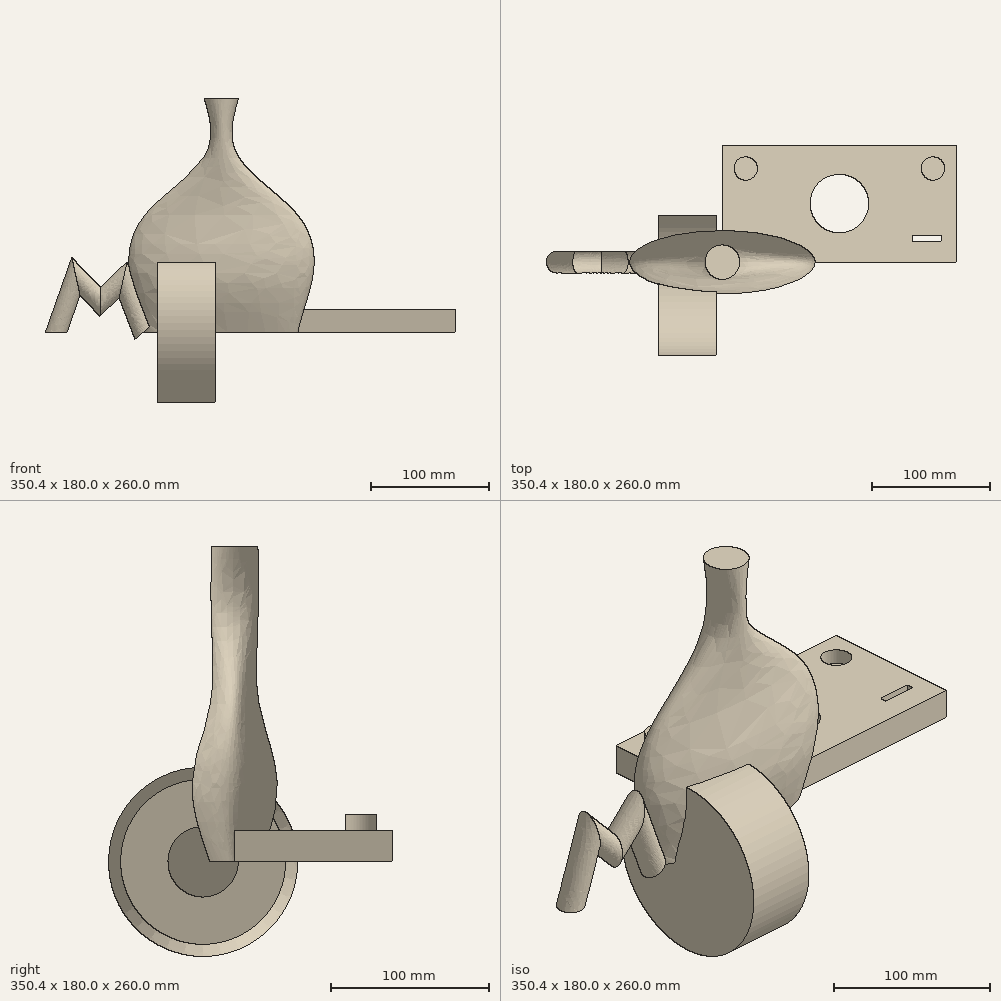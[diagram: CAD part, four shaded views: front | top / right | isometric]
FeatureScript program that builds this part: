
annotation { "Feature Type Name" : "Feature", "Feature Type Description" : "" }
export const myFeature = defineFeature(function(context is Context, id is Id, definition is map)
    precondition{}
    {
        {
            var Q0;
            Q0=qCreatedBy(makeId("Top.planeOp"),FACE);
            var sketch = newSketch(context, id + "F0", { "sketchPlane" : qUnion([Q0])});
            skLineSegment(sketch, "E0.bottom", {"start": v(0, 100) * mm, "end": v(200, 100) * mm});
            skLineSegment(sketch, "E0.top", {"start": v(0, 0) * mm, "end": v(200, 0) * mm});
            skLineSegment(sketch, "E0.left", {"start": v(0, 100) * mm, "end": v(0, 0) * mm});
            skLineSegment(sketch, "E0.right", {"start": v(200, 100) * mm, "end": v(200, 0) * mm});
            skCircle(sketch, "E1", {"center": v(100, 50) * mm, "radius": 25 * mm});
            skSolve(sketch);
        }
        {
            var Q0;
            Q0 = qSketchRegion(id + "F0", true);
            extrude(context, id + "F1", {"entities" : qUnion([Q0]), "depth" : 20 * mm});
        }
        {
            var Q0;
            Q0=makeQuery(id+"F1.opExtrude","CAP_FACE",FACE,{"disambiguationData":[OSD([sQuery(id+"F0.wireOp",EDGE,"E0.bottom"),sQuery(id+"F0.wireOp",EDGE,"E0.top"),sQuery(id+"F0.wireOp",EDGE,"E0.left"),sQuery(id+"F0.wireOp",EDGE,"E0.right"),sQuery(id+"F0.wireOp",EDGE,"E1")])],"isStart":false});
            var sketch = newSketch(context, id + "F2", { "sketchPlane" : qUnion([Q0])});
            skCircle(sketch, "E2", {"center": v(180, 80) * mm, "radius": 10 * mm});
            skSolve(sketch);
        }
        {
            var Q0;
            Q0=makeQuery(id+"F2.imprint","IMPRINT",FACE,{"disambiguationData":[TD([[makeQuery(id+"F2.imprint","IMPRINT",EDGE,{"derivedFrom":sQuery(id+"F2.wireOp",EDGE,"E2")}),1.0]])]});
            extrude(context, id + "F3", {"entities" : qUnion([Q0]), "operationType" : NewBodyOperationType.REMOVE, "oppositeDirection" : true, "depth" : 10 * mm});
        }
        {
            var Q0;
            Q0=makeQuery(id+"F1.opExtrude","CAP_FACE",FACE,{"disambiguationData":[OSD([sQuery(id+"F0.wireOp",EDGE,"E0.bottom"),sQuery(id+"F0.wireOp",EDGE,"E0.top"),sQuery(id+"F0.wireOp",EDGE,"E0.left"),sQuery(id+"F0.wireOp",EDGE,"E0.right"),sQuery(id+"F0.wireOp",EDGE,"E1")])],"isStart":false});
            var sketch = newSketch(context, id + "F4", { "sketchPlane" : qUnion([Q0])});
            skCircle(sketch, "E3", {"center": v(20, 80) * mm, "radius": 10 * mm});
            skSolve(sketch);
        }
        {
            var Q0;
            Q0=makeQuery(id+"F4.imprint","IMPRINT",FACE,{"disambiguationData":[TD([[makeQuery(id+"F4.imprint","IMPRINT",EDGE,{"derivedFrom":sQuery(id+"F4.wireOp",EDGE,"E3")}),1.0]])]});
            extrude(context, id + "F5", {"entities" : qUnion([Q0]), "operationType" : NewBodyOperationType.ADD, "depth" : 10 * mm});
        }
        {
            var Q0;
            Q0=qCreatedBy(makeId("Top.planeOp"),FACE);
            var sketch = newSketch(context, id + "F6", { "sketchPlane" : qUnion([Q0])});
            skLineSegment(sketch, "E4", {"start": v(-20, -20) * mm, "end": v(-55, -20) * mm});
            skLineSegment(sketch, "E5", {"start": v(-55, -20) * mm, "end": v(-55, -80) * mm});
            skLineSegment(sketch, "E6", {"start": v(-55, -80) * mm, "end": v(-5, -80) * mm});
            skLineSegment(sketch, "E7", {"start": v(-5, -80) * mm, "end": v(-49, -72.32) * mm});
            skLineSegment(sketch, "E8", {"start": v(-49, -72.32) * mm, "end": v(-49, -42.32) * mm});
            skArc(sketch, "E9", {"start": v(-20, -20) * mm, "mid": v(-38.3, -26.23) * mm, "end": v(-49, -42.32) * mm});
            skSolve(sketch);
        }
        {
            var Q0;
            Q0=makeQuery(id+"F6.imprint","IMPRINT",FACE,{"disambiguationData":[TD([[makeQuery(id+"F6.imprint","IMPRINT",EDGE,{"derivedFrom":sQuery(id+"F6.wireOp",EDGE,"E4")}),1.0]])]});
            var Q1;
            Q1=sQuery(id+"F6.wireOp",EDGE,"E4");
            revolve(context, id + "F7", {"entities" : qUnion([Q0]), "axis" : qUnion([Q1]), "revolveType" : RevolveType.FULL});
        }
        {
            var Q0;
            Q0=qCreatedBy(makeId("Top.planeOp"),FACE);
            var sketch = newSketch(context, id + "F8", { "sketchPlane" : qUnion([Q0])});
            skCircle(sketch, "E10", {"center": v(-141.12, 0) * mm, "radius": 9.26 * mm});
            skSolve(sketch);
        }
        {
            var Q0;
            Q0=qCreatedBy(makeId("Front.planeOp"),FACE);
            var sketch = newSketch(context, id + "F9", { "sketchPlane" : qUnion([Q0])});
            skLineSegment(sketch, "E11", {"start": v(-141.34, 0) * mm, "end": v(-124.39, 48.03) * mm});
            skLineSegment(sketch, "E12", {"start": v(-124.39, 48.03) * mm, "end": v(-103.39, 26.3) * mm});
            skLineSegment(sketch, "E13", {"start": v(-103.39, 26.3) * mm, "end": v(-83.9, 45.12) * mm});
            skLineSegment(sketch, "E14", {"start": v(-83.9, 45.12) * mm, "end": v(-66.54, 0) * mm});
            skSolve(sketch);
        }
        {
            var Q0;
            Q0=makeQuery(id+"F8.imprint","IMPRINT",FACE,{"disambiguationData":[TD([[makeQuery(id+"F8.imprint","IMPRINT",EDGE,{"derivedFrom":sQuery(id+"F8.wireOp",EDGE,"E10")}),1.0]])]});
            var Q1;
            Q1=sQuery(id+"F9.wireOp",EDGE,"E11");
            var Q2;
            Q2=sQuery(id+"F9.wireOp",EDGE,"E12");
            var Q3;
            Q3=sQuery(id+"F9.wireOp",EDGE,"E13");
            var Q4;
            Q4=sQuery(id+"F9.wireOp",EDGE,"E14");
            sweep(context, id + "F10", {"profiles" : qUnion([Q0]), "path" : qUnion([Q1, Q2, Q3, Q4])});
        }
        {
            var Q0;
            Q0=qCreatedBy(makeId("Top.planeOp"),FACE);
            cPlane(context, id + "F11", {"entities" : qUnion([Q0]), "cplaneType" : CPlaneType.OFFSET, "offset" : 50 * mm, "width" : 150 * mm, "height" : 150 * mm});
        }
        {
            var Q0;
            Q0=qCreatedBy(id+"F11.planeOp",FACE);
            cPlane(context, id + "F12", {"entities" : qUnion([Q0]), "cplaneType" : CPlaneType.OFFSET, "offset" : 50 * mm, "width" : 150 * mm, "height" : 150 * mm});
        }
        {
            var Q0;
            Q0=qCreatedBy(id+"F12.planeOp",FACE);
            cPlane(context, id + "F13", {"entities" : qUnion([Q0]), "cplaneType" : CPlaneType.OFFSET, "offset" : 50 * mm, "width" : 150 * mm, "height" : 150 * mm});
        }
        {
            var Q0;
            Q0=qCreatedBy(makeId("Top.planeOp"),FACE);
            var sketch = newSketch(context, id + "F14", { "sketchPlane" : qUnion([Q0])});
            skEllipse(sketch, "E15", {"center": v(0, 0) * mm, "majorRadius": 65.41 * mm, "minorRadius": 15.83 * mm, "majorAxis": v(1, 0)});
            skSolve(sketch);
        }
        {
            var Q0;
            Q0=qCreatedBy(id+"F11.planeOp",FACE);
            var sketch = newSketch(context, id + "F15", { "sketchPlane" : qUnion([Q0])});
            skEllipse(sketch, "E16", {"center": v(0, 0) * mm, "majorRadius": 78.5 * mm, "minorRadius": 27.08 * mm, "majorAxis": v(1, 0)});
            skSolve(sketch);
        }
        {
            var Q0;
            Q0=qCreatedBy(id+"F12.planeOp",FACE);
            var sketch = newSketch(context, id + "F16", { "sketchPlane" : qUnion([Q0])});
            skEllipse(sketch, "E17", {"center": v(0, 0) * mm, "majorRadius": 65.42 * mm, "minorRadius": 15.55 * mm, "majorAxis": v(1, 0)});
            skSolve(sketch);
        }
        {
            var Q0;
            Q0=qCreatedBy(id+"F13.planeOp",FACE);
            var sketch = newSketch(context, id + "F17", { "sketchPlane" : qUnion([Q0])});
            skCircle(sketch, "E18", {"center": v(0, 0) * mm, "radius": 14.74 * mm});
            skSolve(sketch);
        }
        {
            var Q0;
            Q0=qCreatedBy(id+"F13.planeOp",FACE);
            cPlane(context, id + "F18", {"entities" : qUnion([Q0]), "cplaneType" : CPlaneType.OFFSET, "offset" : 50 * mm, "width" : 150 * mm, "height" : 150 * mm});
        }
        {
            var Q0;
            Q0=qCreatedBy(id+"F18.planeOp",FACE);
            var sketch = newSketch(context, id + "F19", { "sketchPlane" : qUnion([Q0])});
            skCircle(sketch, "E19.0", {"center": v(0, 0) * mm, "radius": 14.74 * mm});
            skSolve(sketch);
        }
        {
            var Q0;
            Q0=makeQuery(id+"F14.imprint","IMPRINT",FACE,{"disambiguationData":[TD([[makeQuery(id+"F14.imprint","IMPRINT",EDGE,{"derivedFrom":sQuery(id+"F14.wireOp",EDGE,"E15")}),1.0]])]});
            var Q1;
            Q1=makeQuery(id+"F15.imprint","IMPRINT",FACE,{"disambiguationData":[TD([[makeQuery(id+"F15.imprint","IMPRINT",EDGE,{"derivedFrom":sQuery(id+"F15.wireOp",EDGE,"E16")}),1.0]])]});
            var Q2;
            Q2=makeQuery(id+"F16.imprint","IMPRINT",FACE,{"disambiguationData":[TD([[makeQuery(id+"F16.imprint","IMPRINT",EDGE,{"derivedFrom":sQuery(id+"F16.wireOp",EDGE,"E17")}),1.0]])]});
            var Q3;
            Q3=makeQuery(id+"F17.imprint","IMPRINT",FACE,{"disambiguationData":[TD([[makeQuery(id+"F17.imprint","IMPRINT",EDGE,{"derivedFrom":sQuery(id+"F17.wireOp",EDGE,"E18")}),1.0]])]});
            var Q4;
            Q4=makeQuery(id+"F19.imprint","IMPRINT",FACE,{"disambiguationData":[TD([[makeQuery(id+"F19.imprint","IMPRINT",EDGE,{"derivedFrom":sQuery(id+"F19.wireOp",EDGE,"E19.0")}),1.0]])]});
            loft(context, id + "F20", {"sheetProfilesArray" : [{ "sheetProfileEntities" : qUnion([Q0]) }, { "sheetProfileEntities" : qUnion([Q1]) }, { "sheetProfileEntities" : qUnion([Q2]) }, { "sheetProfileEntities" : qUnion([Q3]) }, { "sheetProfileEntities" : qUnion([Q4]) }]});
        }
        {
            var Q0;
            Q0=makeQuery(id+"F1.opExtrude","CAP_FACE",FACE,{"disambiguationData":[OSD([sQuery(id+"F0.wireOp",EDGE,"E0.bottom"),sQuery(id+"F0.wireOp",EDGE,"E0.top"),sQuery(id+"F0.wireOp",EDGE,"E0.left"),sQuery(id+"F0.wireOp",EDGE,"E0.right"),sQuery(id+"F0.wireOp",EDGE,"E1")])],"isStart":false});
            var sketch = newSketch(context, id + "F21", { "sketchPlane" : qUnion([Q0])});
            skLineSegment(sketch, "E20.bottom", {"start": v(162.8, 17.77) * mm, "end": v(187.29, 17.77) * mm});
            skLineSegment(sketch, "E20.top", {"start": v(162.8, 23) * mm, "end": v(187.29, 23) * mm});
            skLineSegment(sketch, "E20.left", {"start": v(162.8, 17.77) * mm, "end": v(162.8, 23) * mm});
            skLineSegment(sketch, "E20.right", {"start": v(187.29, 17.77) * mm, "end": v(187.29, 23) * mm});
            skSolve(sketch);
        }
        {
            var Q0;
            Q0=makeQuery(id+"F21.imprint","IMPRINT",FACE,{"disambiguationData":[TD([[makeQuery(id+"F21.imprint","IMPRINT",EDGE,{"derivedFrom":sQuery(id+"F21.wireOp",EDGE,"E20.bottom")}),1.0]])]});
            extrude(context, id + "F22", {"entities" : qUnion([Q0]), "operationType" : NewBodyOperationType.REMOVE, "oppositeDirection" : true, "depth" : 25 * mm});
        }
    });
